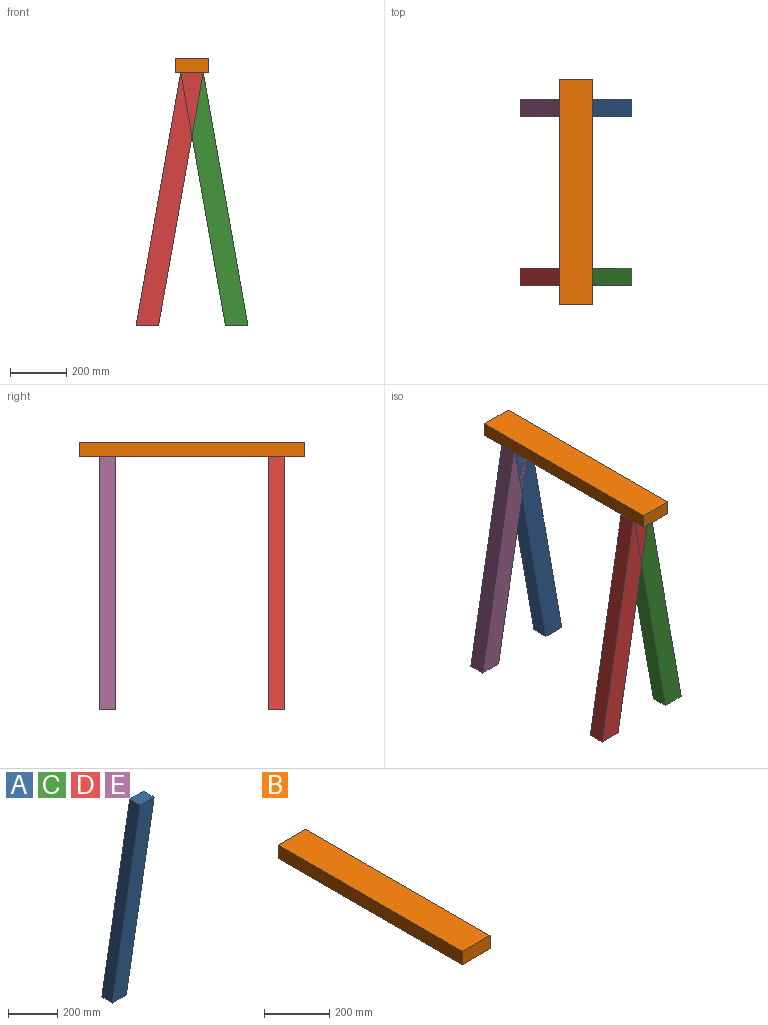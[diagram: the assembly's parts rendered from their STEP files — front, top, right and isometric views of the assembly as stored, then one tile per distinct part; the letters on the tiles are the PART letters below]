
ASSEMBLY  parts=5 mates=4
PART A: 6 faces, bbox 238.7x60x900 mm
  f0: plane 80x60mm, normal (0,0,1), area 4800mm2, adj f1,f3,f4,f5
  f1: plane 900x158.69mm, normal (-0.98,0,0.17), area 54833mm2, adj f0,f2,f4,f5
  f2: plane 80x60mm, normal (0,0,-1), area 4800mm2, adj f1,f3,f4,f5
  f3: plane 900x158.69mm, normal (0.98,0,-0.17), area 54833mm2, adj f0,f2,f4,f5
  f4: plane 900x238.69mm, normal (0,-1,0), area 72000mm2, adj f0,f1,f2,f3
  f5: plane 900x238.69mm, normal (0,1,0), area 72000mm2, adj f0,f1,f2,f3
PART B: 6 faces, bbox 120x800x50 mm
  f0: plane 800x120mm, normal (0,0,1), area 96000mm2, adj f1,f3,f4,f5
  f1: plane 800x50mm, normal (-1,0,0), area 40000mm2, adj f0,f2,f4,f5
  f2: plane 800x120mm, normal (0,0,-1), area 96000mm2, adj f1,f3,f4,f5
  f3: plane 800x50mm, normal (1,0,0), area 40000mm2, adj f0,f2,f4,f5
  f4: plane 120x50mm, normal (0,1,0), area 6000mm2, adj f0,f1,f2,f3
  f5: plane 120x50mm, normal (0,-1,0), area 6000mm2, adj f0,f1,f2,f3
PART C: same geometry as A
PART D: same geometry as A
PART E: same geometry as A
PLACE A rot(axis=(0,0,1),180deg) t=(-324.96,-216.82,-58.44)mm
PLACE B t=(-344.96,-886.82,-8.44)mm
PLACE C rot(axis=(0,0,1),180deg) t=(-324.96,-816.82,-58.44)mm
PLACE D t=(-244.96,-756.82,-58.44)mm
PLACE E t=(-244.96,-156.82,-58.44)mm
MATE planar A.f0 <-> E.f0  axis (0,0,1) through (-284.96,-186.82,-58.44)mm
MATE planar E.f0 <-> B.f2  axis (0,0,1) through (-284.96,-186.82,-58.44)mm
MATE planar D.f0 <-> B.f2  axis (0,0,1) through (-284.96,-786.82,-58.44)mm
MATE planar C.f0 <-> B.f2  axis (0,0,1) through (-284.96,-786.82,-58.44)mm
